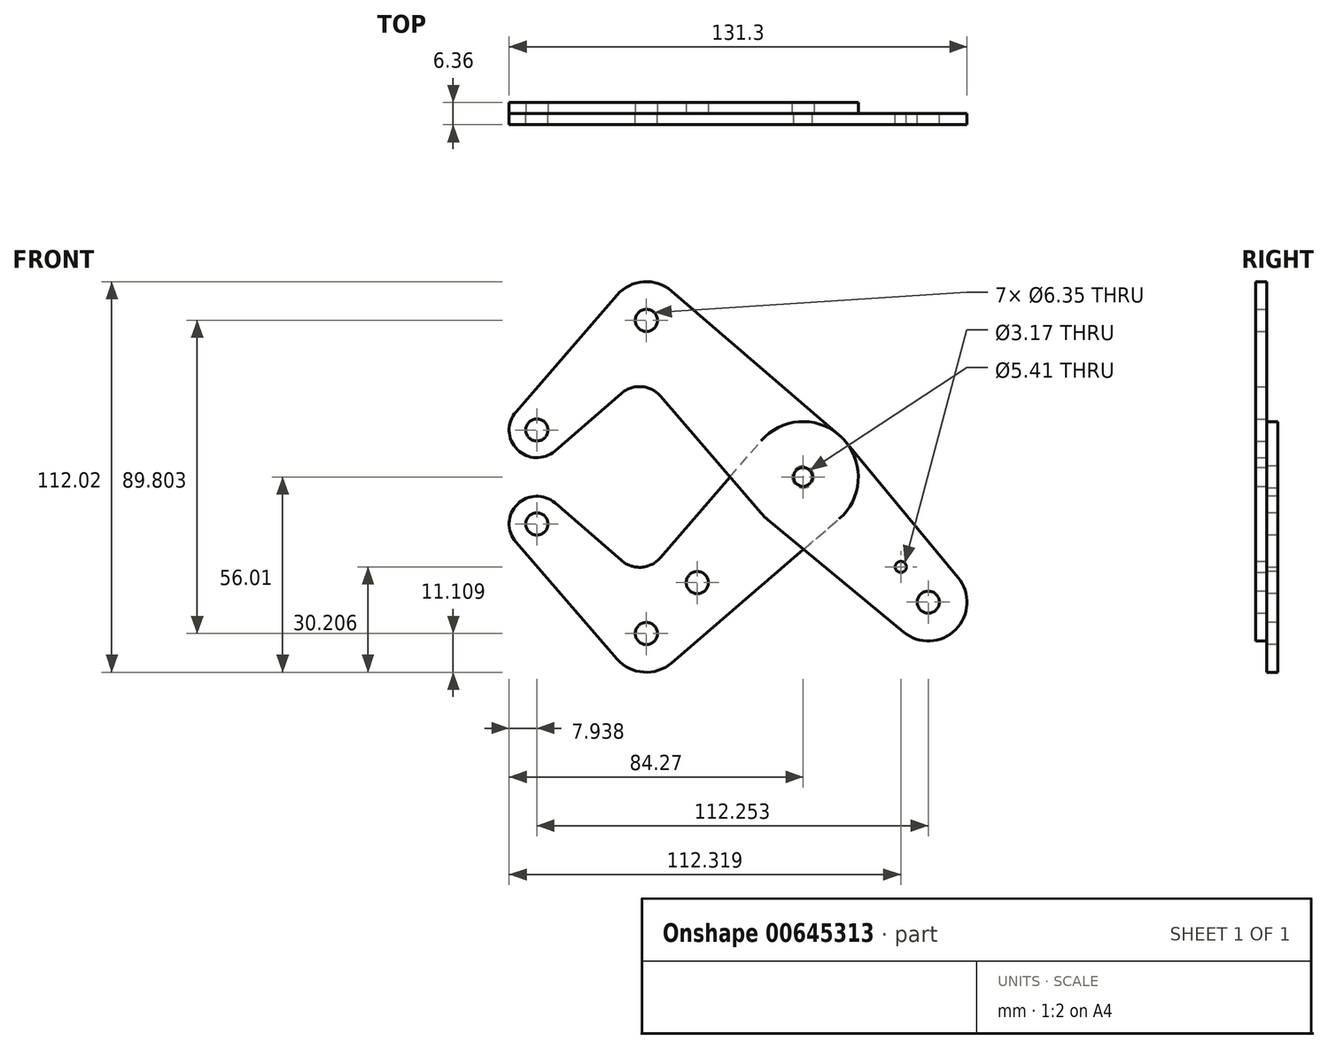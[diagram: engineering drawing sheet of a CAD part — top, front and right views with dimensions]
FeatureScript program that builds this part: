
annotation { "Feature Type Name" : "Feature", "Feature Type Description" : "" }
export const myFeature = defineFeature(function(context is Context, id is Id, definition is map)
    precondition{}
    {
        {
            var Q0;
            Q0=qCreatedBy(makeId("Front.planeOp"),FACE);
            var sketch = newSketch(context, id + "F0", { "sketchPlane" : qUnion([Q0])});
            skLineSegment(sketch, "E0", {"start": v(-76.33, 13.47) * mm, "end": v(-44.9, 44.9) * mm, "construction": true});
            skLineSegment(sketch, "E1", {"start": v(-44.9, 44.9) * mm, "end": v(35.92, -35.92) * mm, "construction": true});
            skCircle(sketch, "E2", {"center": v(-76.33, 13.47) * mm, "radius": 7.94 * mm});
            skCircle(sketch, "E3", {"center": v(-44.9, 44.9) * mm, "radius": 11.11 * mm});
            skCircle(sketch, "E4", {"center": v(-44.9, 44.9) * mm, "radius": 3.18 * mm});
            skCircle(sketch, "E5", {"center": v(0, 0) * mm, "radius": 15.88 * mm});
            skCircle(sketch, "E6", {"center": v(0, 0) * mm, "radius": 2.7 * mm});
            skCircle(sketch, "E7", {"center": v(35.92, -35.92) * mm, "radius": 11.11 * mm});
            skCircle(sketch, "E8", {"center": v(35.92, -35.92) * mm, "radius": 3.18 * mm});
            skCircle(sketch, "E9", {"center": v(-76.33, 13.47) * mm, "radius": 3.18 * mm});
            skCircle(sketch, "E10", {"center": v(0, 0) * mm, "radius": 3.18 * mm});
            skCircle(sketch, "E11", {"center": v(28.05, -25.8) * mm, "radius": 1.59 * mm});
            skLineSegment(sketch, "E12", {"start": v(-53.3, 52.18) * mm, "end": v(-82.33, 18.67) * mm});
            skLineSegment(sketch, "E13", {"start": v(-52.08, 23.98) * mm, "end": v(-71.13, 7.47) * mm});
            skArc(sketch, "E14.filletArc", {"start": v(-40.85, 23.15) * mm, "mid": v(-46.3, 25.9) * mm, "end": v(-52.08, 23.98) * mm});
            skLineSegment(sketch, "E15", {"start": v(0, 0) * mm, "end": v(-44.9, -44.9) * mm, "construction": true});
            skLineSegment(sketch, "E16", {"start": v(-44.9, -44.9) * mm, "end": v(-76.33, -13.47) * mm, "construction": true});
            skCircle(sketch, "E17", {"center": v(-76.33, -13.47) * mm, "radius": 7.94 * mm});
            skCircle(sketch, "E18", {"center": v(-76.33, -13.47) * mm, "radius": 3.18 * mm});
            skCircle(sketch, "E19", {"center": v(-44.9, -44.9) * mm, "radius": 11.11 * mm});
            skCircle(sketch, "E20", {"center": v(-44.9, -44.9) * mm, "radius": 3.18 * mm});
            skCircle(sketch, "E21", {"center": v(-30.3, -30.3) * mm, "radius": 3.18 * mm});
            skLineSegment(sketch, "E22", {"start": v(-71.13, -7.47) * mm, "end": v(-52.08, -23.98) * mm});
            skLineSegment(sketch, "E23", {"start": v(-82.33, -18.67) * mm, "end": v(-53.3, -52.18) * mm});
            skLineSegment(sketch, "E24", {"start": v(-40.85, -23.15) * mm, "end": v(-11.26, 11.26) * mm});
            skLineSegment(sketch, "E25", {"start": v(-37.66, -53.33) * mm, "end": v(11.26, -11.26) * mm});
            skArc(sketch, "E26.filletArc", {"start": v(-52.08, -23.98) * mm, "mid": v(-46.3, -25.9) * mm, "end": v(-40.85, -23.15) * mm});
            skLineSegment(sketch, "E27", {"start": v(10.35, 12.04) * mm, "end": v(-37.66, 53.33) * mm});
            skLineSegment(sketch, "E28", {"start": v(-53.33, 37.66) * mm, "end": v(-12.04, -10.35) * mm});
            skLineSegment(sketch, "E29", {"start": v(-10.12, -12.23) * mm, "end": v(28.83, -44.48) * mm});
            skLineSegment(sketch, "E30", {"start": v(44.48, -28.83) * mm, "end": v(12.23, 10.12) * mm});
            skSolve(sketch);
        }
        {
            var Q0;
            Q0=makeQuery(id+"F0.imprint","IMPRINT",FACE,{"disambiguationData":[TD([[makeQuery(id+"F0.imprint","IMPRINT",EDGE,{"derivedFrom":sQuery(id+"F0.wireOp",EDGE,"E9")}),-1.0]])]});
            var Q1;
            Q1=makeQuery(id+"F0.imprint","IMPRINT",FACE,{"disambiguationData":[TD([[makeQuery(id+"F0.imprint","IMPRINT",EDGE,{"derivedFrom":sQuery(id+"F0.wireOp",EDGE,"E4")}),-1.0]])]});
            var Q2;
            {var subQ0=sQuery(id+"F0.wireOp",EDGE,"E12");Q2=makeQuery(id+"F0.imprint","IMPRINT",FACE,{"disambiguationData":[TD([[makeQuery(id+"F0.imprint","IMPRINT",EDGE,{"derivedFrom":subQ0}),1.0]])]});}
            var Q3;
            {var subQ0=sQuery(id+"F0.wireOp",EDGE,"E24");var subQ1=sQuery(id+"F0.wireOp",EDGE,"E5");var subQ2=makeQuery(id+"F0.imprint","INTERSECT",VERTEX,{"derivedFrom":[subQ1,subQ0]});Q3=makeQuery(id+"F0.imprint","IMPRINT",FACE,{"disambiguationData":[TD([[makeQuery(id+"F0.imprint","IMPRINT",EDGE,{"disambiguationData":[TD([[subQ2,-1.0]])],"derivedFrom":subQ1}),-1.0]])]});}
            var Q4;
            Q4=makeQuery(id+"F0.imprint","IMPRINT",FACE,{"disambiguationData":[TD([[makeQuery(id+"F0.imprint","IMPRINT",EDGE,{"derivedFrom":sQuery(id+"F0.wireOp",EDGE,"E10")}),-1.0]])]});
            var Q5;
            Q5=makeQuery(id+"F0.imprint","IMPRINT",FACE,{"disambiguationData":[TD([[makeQuery(id+"F0.imprint","IMPRINT",EDGE,{"derivedFrom":sQuery(id+"F0.wireOp",EDGE,"E6")}),-1.0]])]});
            var Q6;
            Q6=makeQuery(id+"F0.imprint","IMPRINT",FACE,{"disambiguationData":[TD([[makeQuery(id+"F0.imprint","IMPRINT",EDGE,{"derivedFrom":sQuery(id+"F0.wireOp",EDGE,"E11")}),-1.0]])]});
            var Q7;
            {var subQ0=sQuery(id+"F0.wireOp",EDGE,"E25");var subQ1=sQuery(id+"F0.wireOp",EDGE,"E5");var subQ2=makeQuery(id+"F0.imprint","INTERSECT",VERTEX,{"derivedFrom":[subQ1,subQ0]});Q7=makeQuery(id+"F0.imprint","IMPRINT",FACE,{"disambiguationData":[TD([[makeQuery(id+"F0.imprint","IMPRINT",EDGE,{"disambiguationData":[TD([[subQ2,1.0]])],"derivedFrom":subQ1}),-1.0]])]});}
            var Q8;
            Q8=makeQuery(id+"F0.imprint","IMPRINT",FACE,{"disambiguationData":[TD([[makeQuery(id+"F0.imprint","IMPRINT",EDGE,{"derivedFrom":sQuery(id+"F0.wireOp",EDGE,"E8")}),-1.0]])]});
            var Q9;
            {var subQ0=sQuery(id+"F0.wireOp",EDGE,"E27");Q9=makeQuery(id+"F0.imprint","IMPRINT",FACE,{"disambiguationData":[TD([[makeQuery(id+"F0.imprint","IMPRINT",EDGE,{"derivedFrom":subQ0}),1.0]])]});}
            extrude(context, id + "F1", {"entities" : qUnion([Q0, Q1, Q2, Q3, Q4, Q5, Q6, Q7, Q8, Q9]), "depth" : 3.17 * mm, "offsetDistance" : 25.4 * mm});
        }
        {
            var Q0;
            Q0=makeQuery(id+"F0.imprint","IMPRINT",FACE,{"disambiguationData":[TD([[makeQuery(id+"F0.imprint","IMPRINT",EDGE,{"derivedFrom":sQuery(id+"F0.wireOp",EDGE,"E20")}),-1.0]])]});
            var Q1;
            Q1=makeQuery(id+"F0.imprint","IMPRINT",FACE,{"disambiguationData":[TD([[makeQuery(id+"F0.imprint","IMPRINT",EDGE,{"derivedFrom":sQuery(id+"F0.wireOp",EDGE,"E10")}),-1.0]])]});
            var Q2;
            {var subQ0=sQuery(id+"F0.wireOp",EDGE,"E24");var subQ1=sQuery(id+"F0.wireOp",EDGE,"E5");var subQ2=makeQuery(id+"F0.imprint","INTERSECT",VERTEX,{"derivedFrom":[subQ1,subQ0]});Q2=makeQuery(id+"F0.imprint","IMPRINT",FACE,{"disambiguationData":[TD([[makeQuery(id+"F0.imprint","IMPRINT",EDGE,{"disambiguationData":[TD([[subQ2,-1.0]])],"derivedFrom":subQ1}),-1.0]])]});}
            var Q3;
            {var subQ0=sQuery(id+"F0.wireOp",EDGE,"E25");var subQ1=sQuery(id+"F0.wireOp",EDGE,"E5");var subQ2=makeQuery(id+"F0.imprint","INTERSECT",VERTEX,{"derivedFrom":[subQ1,subQ0]});Q3=makeQuery(id+"F0.imprint","IMPRINT",FACE,{"disambiguationData":[TD([[makeQuery(id+"F0.imprint","IMPRINT",EDGE,{"disambiguationData":[TD([[subQ2,1.0]])],"derivedFrom":subQ1}),-1.0]])]});}
            var Q4;
            Q4=makeQuery(id+"F0.imprint","IMPRINT",FACE,{"disambiguationData":[TD([[makeQuery(id+"F0.imprint","IMPRINT",EDGE,{"derivedFrom":sQuery(id+"F0.wireOp",EDGE,"E18")}),-1.0]])]});
            var Q5;
            Q5=makeQuery(id+"F0.imprint","IMPRINT",FACE,{"disambiguationData":[TD([[makeQuery(id+"F0.imprint","IMPRINT",EDGE,{"derivedFrom":sQuery(id+"F0.wireOp",EDGE,"E21")}),-1.0]])]});
            extrude(context, id + "F2", {"entities" : qUnion([Q0, Q1, Q2, Q3, Q4, Q5]), "oppositeDirection" : true, "depth" : 3.17 * mm, "offsetDistance" : 25.4 * mm});
        }
    });
